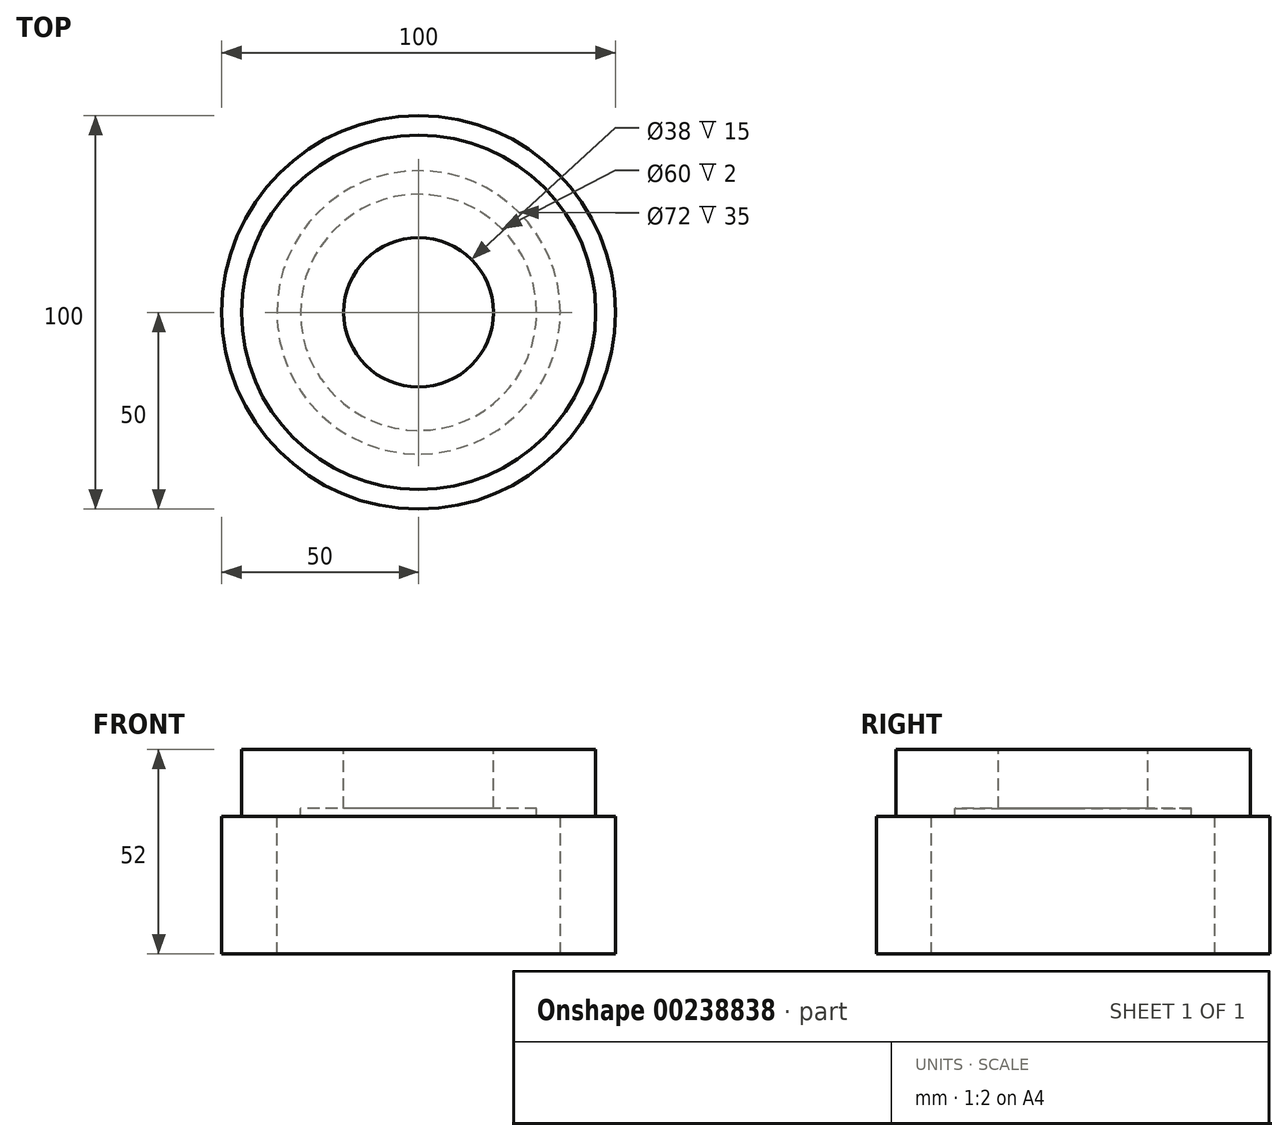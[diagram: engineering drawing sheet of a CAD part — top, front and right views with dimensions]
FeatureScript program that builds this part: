
annotation { "Feature Type Name" : "Feature", "Feature Type Description" : "" }
export const myFeature = defineFeature(function(context is Context, id is Id, definition is map)
    precondition{}
    {
        {
            var Q0;
            Q0=qCreatedBy(makeId("Front.planeOp"),FACE);
            var sketch = newSketch(context, id + "F0", { "sketchPlane" : qUnion([Q0])});
            skLineSegment(sketch, "E0", {"start": v(0, 48.41) * mm, "end": v(0, -44.43) * mm, "construction": true});
            skLineSegment(sketch, "E1", {"start": v(19, 31.35) * mm, "end": v(19, 16.35) * mm});
            skLineSegment(sketch, "E2", {"start": v(19, 16.35) * mm, "end": v(30, 16.35) * mm});
            skLineSegment(sketch, "E3", {"start": v(30, 16.35) * mm, "end": v(30, 14.35) * mm});
            skLineSegment(sketch, "E4", {"start": v(30, 14.35) * mm, "end": v(36, 14.35) * mm});
            skLineSegment(sketch, "E5", {"start": v(36, 14.35) * mm, "end": v(36, -20.65) * mm});
            skLineSegment(sketch, "E6", {"start": v(36, -20.65) * mm, "end": v(50, -20.65) * mm});
            skLineSegment(sketch, "E7", {"start": v(50, -20.65) * mm, "end": v(50, 14.35) * mm});
            skLineSegment(sketch, "E8", {"start": v(50, 14.35) * mm, "end": v(45, 14.35) * mm});
            skLineSegment(sketch, "E9", {"start": v(45, 14.35) * mm, "end": v(45, 31.35) * mm});
            skLineSegment(sketch, "E10", {"start": v(45, 31.35) * mm, "end": v(19, 31.35) * mm});
            skSolve(sketch);
        }
        {
            var Q0;
            Q0=makeQuery(id+"F0.imprint","IMPRINT",FACE,{"disambiguationData":[TD([[makeQuery(id+"F0.imprint","IMPRINT",EDGE,{"derivedFrom":sQuery(id+"F0.wireOp",EDGE,"E1")}),1.0]])]});
            var Q1;
            Q1=sQuery(id+"F0.wireOp",EDGE,"E0");
            revolve(context, id + "F1", {"entities" : qUnion([Q0]), "axis" : qUnion([Q1]), "revolveType" : RevolveType.FULL});
        }
    });
